# Revit family: Oxel Side Post Galvanised – Cast In Place
name_source: partatom
category: Furniture
units: mm (PartAtom-declared; Revit-internal decimal feet)

## family parameters
Always vertical = Yes
Cut with Voids When Loaded = No
OmniClass Number = 23.21.23.13.15
Room Calculation Point = No
Shared = No
Work Plane-Based = No

## types (2) — shared parameters
Body material = Hags - Steel - Galvanized
Body material_90 = Hags - Steel - Galvanized
Construction material = Hags - Steel - Galvanized
Description = Sofa Sofiero Detached
Edition number = 1
IFC Classification = Furniture
Manufacturer = Hags
Manufacturer name = HAGS
OmniClass Code = 23-21 23 13 15
Product Guid = 90e49432-c870-4a59-897e-b15016e8f9bd
QR code = https://www.hags.com
URL = https://www.hags.com
Uniclass 1.4 Code = L8211
Uniclass 1.4 Description = Furniture
zero-valued in all types: Default Elevation

## per-type parameters (varying)
| type | BIMobject category | Model | OmniClass Description | Product SKU | Product data url | Product name | Product url |
| 8000116 / Galvanized | Litter Bins | 8000116 | Residential Litter Bins | Litter_Bin_Oxel_Detached | https://www.hags.com | Oxel Side Post Galvanised Cast In Place | https://www.hags.com |
| 8037716 / Galvanized | Bench & Park Bench | 8037014 | Residential Sofas | Table_Ekeby_Detached | https://bimobject.com | Ekeby Table Cast In Place | https://hags.se |

## geometry (parser evidence)
native form markers: Sweep x2
no freeform markers — native parametric forms only
